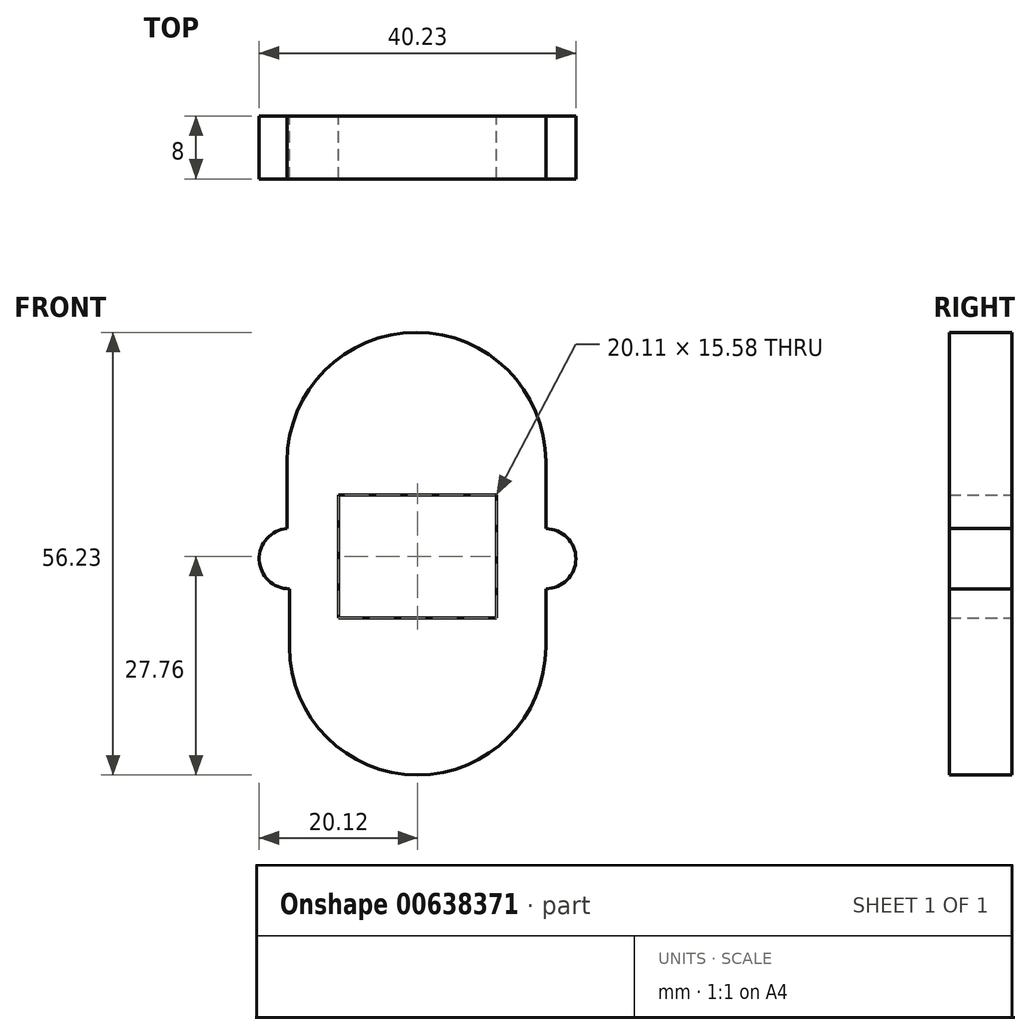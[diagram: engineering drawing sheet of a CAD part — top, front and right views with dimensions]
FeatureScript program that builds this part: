
annotation { "Feature Type Name" : "Feature", "Feature Type Description" : "" }
export const myFeature = defineFeature(function(context is Context, id is Id, definition is map)
    precondition{}
    {
        {
            var Q0;
            Q0=qCreatedBy(makeId("Front.planeOp"),FACE);
            var sketch = newSketch(context, id + "F0", { "sketchPlane" : qUnion([Q0])});
            skLineSegment(sketch, "E0.bottom", {"start": v(10.06, -7.8) * mm, "end": v(-10.06, -7.8) * mm});
            skLineSegment(sketch, "E0.top", {"start": v(10.06, 7.8) * mm, "end": v(-10.06, 7.8) * mm});
            skLineSegment(sketch, "E0.left", {"start": v(10.06, -7.8) * mm, "end": v(10.06, 7.8) * mm});
            skLineSegment(sketch, "E0.right", {"start": v(-10.06, -7.8) * mm, "end": v(-10.06, 7.8) * mm});
            skPoint(sketch, "E0.middle", {"position": v(0, 0) * mm});
            skLineSegment(sketch, "E1.bottom", {"start": v(16.29, 12.04) * mm, "end": v(3.82, 12.04) * mm});
            skLineSegment(sketch, "E1.top", {"start": v(16.29, 3.54) * mm, "end": v(3.82, 3.54) * mm});
            skLineSegment(sketch, "E1.left", {"start": v(16.29, 12.04) * mm, "end": v(16.29, 3.54) * mm});
            skLineSegment(sketch, "E1.right", {"start": v(3.82, 12.04) * mm, "end": v(3.82, 3.54) * mm});
            skPoint(sketch, "E1.middle", {"position": v(10.06, 7.8) * mm});
            skLineSegment(sketch, "E2.bottom", {"start": v(-16.57, 12.04) * mm, "end": v(-3.54, 12.04) * mm});
            skLineSegment(sketch, "E2.top", {"start": v(-16.57, 3.54) * mm, "end": v(-3.54, 3.54) * mm});
            skLineSegment(sketch, "E2.left", {"start": v(-16.57, 12.04) * mm, "end": v(-16.57, 3.54) * mm});
            skLineSegment(sketch, "E2.right", {"start": v(-3.54, 12.04) * mm, "end": v(-3.54, 3.54) * mm});
            skPoint(sketch, "E2.middle", {"position": v(-10.06, 7.8) * mm});
            skLineSegment(sketch, "E3.bottom", {"start": v(-16.29, -11.47) * mm, "end": v(-3.82, -11.47) * mm});
            skLineSegment(sketch, "E3.top", {"start": v(-16.29, -4.1) * mm, "end": v(-3.82, -4.1) * mm});
            skLineSegment(sketch, "E3.left", {"start": v(-16.29, -11.47) * mm, "end": v(-16.29, -4.1) * mm});
            skLineSegment(sketch, "E3.right", {"start": v(-3.82, -11.47) * mm, "end": v(-3.82, -4.1) * mm});
            skPoint(sketch, "E3.middle", {"position": v(-10.06, -7.8) * mm});
            skLineSegment(sketch, "E4.bottom", {"start": v(16.29, -11.47) * mm, "end": v(3.82, -11.47) * mm});
            skLineSegment(sketch, "E4.top", {"start": v(16.29, -4.1) * mm, "end": v(3.82, -4.1) * mm});
            skLineSegment(sketch, "E4.left", {"start": v(16.29, -11.47) * mm, "end": v(16.29, -4.1) * mm});
            skLineSegment(sketch, "E4.right", {"start": v(3.82, -11.47) * mm, "end": v(3.82, -4.1) * mm});
            skPoint(sketch, "E4.middle", {"position": v(10.06, -7.8) * mm});
            skArc(sketch, "E5", {"start": v(16.29, 12.04) * mm, "mid": v(-0.14, 28.47) * mm, "end": v(-16.57, 12.04) * mm});
            skArc(sketch, "E6", {"start": v(-16.29, -11.47) * mm, "mid": v(0, -27.76) * mm, "end": v(16.29, -11.47) * mm});
            skArc(sketch, "E7", {"start": v(-16.57, 3.54) * mm, "mid": v(-20.12, -0.42) * mm, "end": v(-16.29, -4.1) * mm});
            skArc(sketch, "E8", {"start": v(16.29, -4.1) * mm, "mid": v(20.11, -0.28) * mm, "end": v(16.29, 3.54) * mm});
            skSolve(sketch);
        }
        {
            var Q0;
            Q0 = qSketchRegion(id + "F0", true);
            extrude(context, id + "F1", {"entities" : qUnion([Q0]), "depth" : 8 * mm, "offsetDistance" : 25 * mm});
        }
    });
